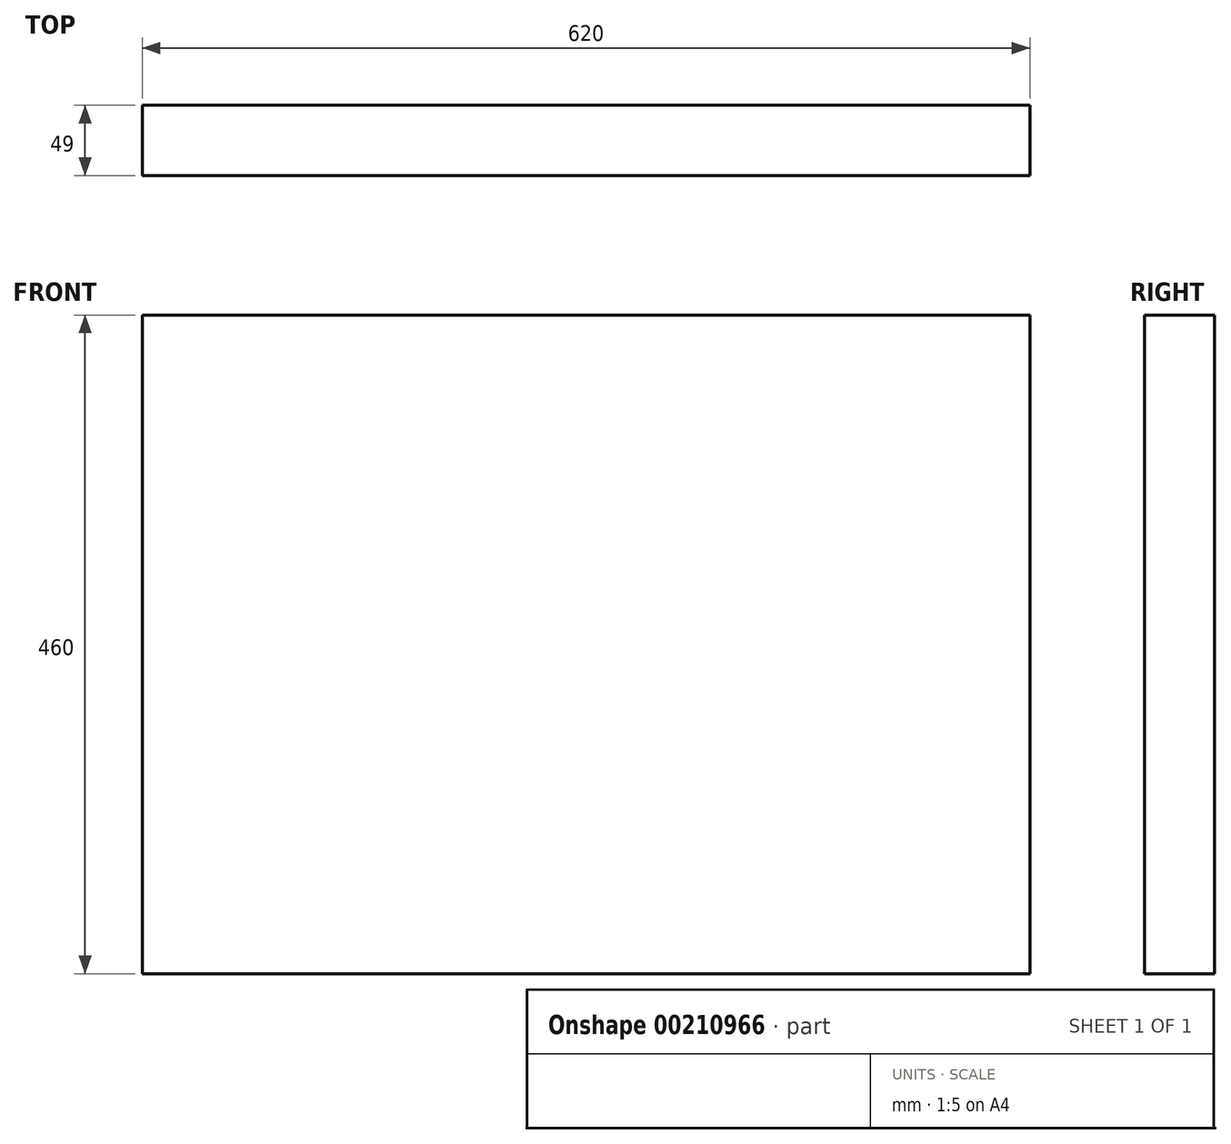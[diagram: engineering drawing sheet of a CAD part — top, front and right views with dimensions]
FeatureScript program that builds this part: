
annotation { "Feature Type Name" : "Feature", "Feature Type Description" : "" }
export const myFeature = defineFeature(function(context is Context, id is Id, definition is map)
    precondition{}
    {
        {
            var Q0;
            Q0=qCreatedBy(makeId("Front.planeOp"),FACE);
            var sketch = newSketch(context, id + "F0", { "sketchPlane" : qUnion([Q0])});
            skLineSegment(sketch, "E0.bottom", {"start": v(310, -230) * mm, "end": v(-310, -230) * mm});
            skLineSegment(sketch, "E0.top", {"start": v(310, 230) * mm, "end": v(-310, 230) * mm});
            skLineSegment(sketch, "E0.left", {"start": v(310, -230) * mm, "end": v(310, 230) * mm});
            skLineSegment(sketch, "E0.right", {"start": v(-310, -230) * mm, "end": v(-310, 230) * mm});
            skPoint(sketch, "E0.middle", {"position": v(0, 0) * mm});
            skSolve(sketch);
        }
        {
            var Q0;
            Q0=makeQuery(id+"F0.imprint","IMPRINT",FACE,{"disambiguationData":[TD([[makeQuery(id+"F0.imprint","IMPRINT",EDGE,{"derivedFrom":sQuery(id+"F0.wireOp",EDGE,"E0.bottom")}),-1.0]])]});
            extrude(context, id + "F1", {"entities" : qUnion([Q0]), "depth" : 49 * mm});
        }
    });
